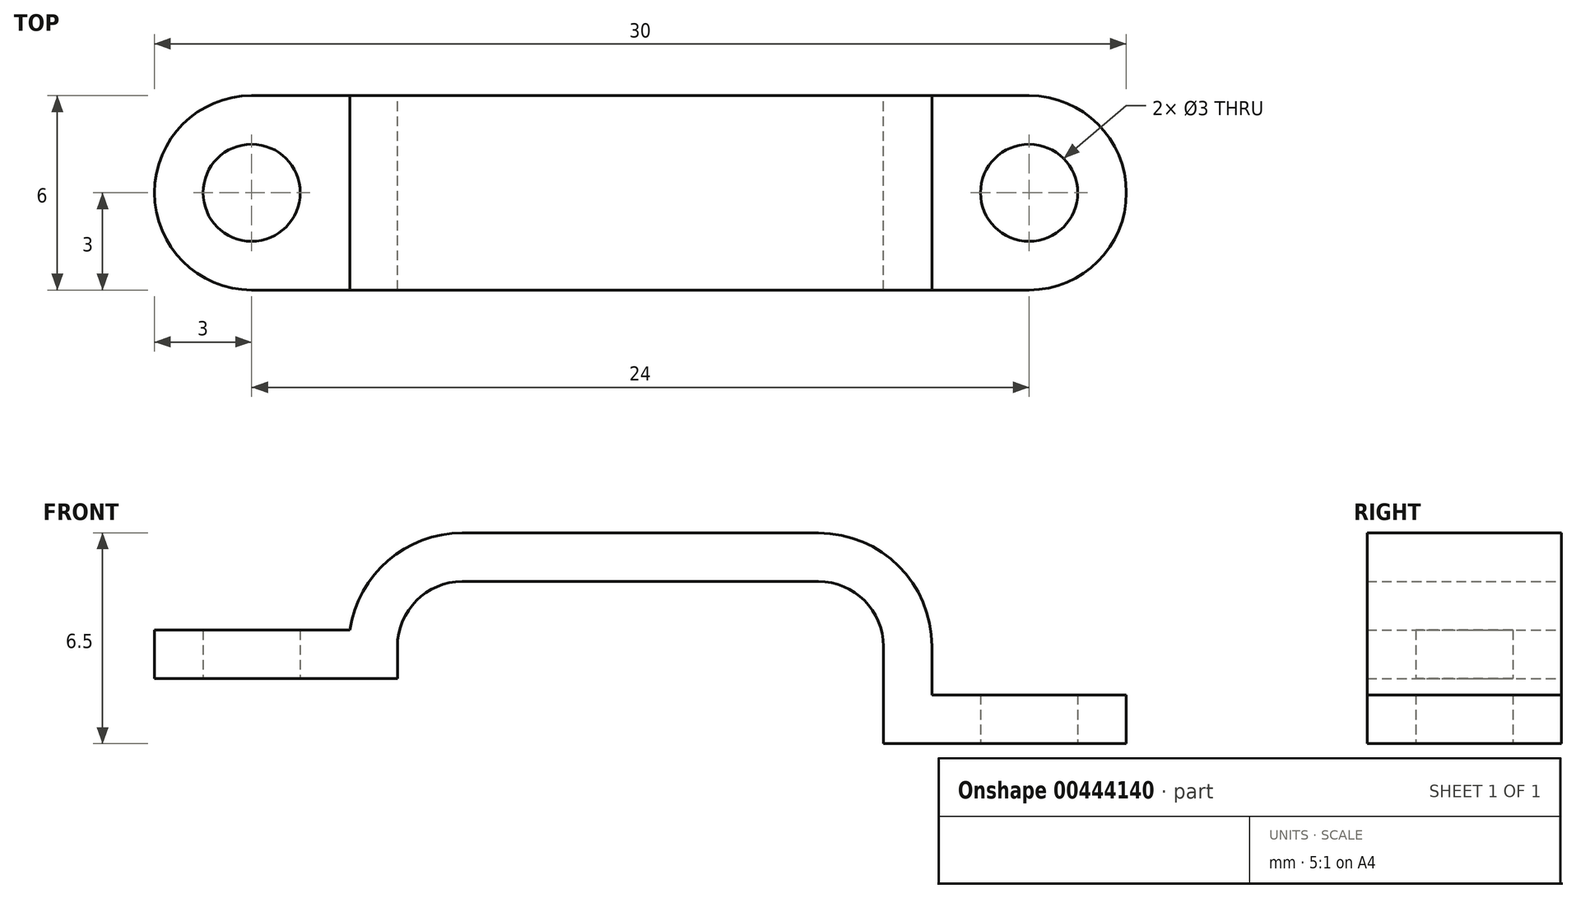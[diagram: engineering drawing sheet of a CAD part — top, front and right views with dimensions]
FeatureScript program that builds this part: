
annotation { "Feature Type Name" : "Feature", "Feature Type Description" : "" }
export const myFeature = defineFeature(function(context is Context, id is Id, definition is map)
    precondition{}
    {
        {
            var Q0;
            Q0=qCreatedBy(makeId("Front.planeOp"),FACE);
            var sketch = newSketch(context, id + "F0", { "sketchPlane" : qUnion([Q0])});
            skLineSegment(sketch, "E0.bottom", {"start": v(0, 0) * mm, "end": v(15, 0) * mm});
            skLineSegment(sketch, "E0.top", {"start": v(2, 5) * mm, "end": v(13, 5) * mm});
            skLineSegment(sketch, "E0.left", {"start": v(0, 0) * mm, "end": v(0, 3) * mm});
            skLineSegment(sketch, "E0.right", {"start": v(15, 0) * mm, "end": v(15, 3) * mm});
            skPoint(sketch, "E1.visualSharp", {"position": v(0, 5) * mm});
            skArc(sketch, "E1.filletArc", {"start": v(2, 5) * mm, "mid": v(0.59, 4.41) * mm, "end": v(0, 3) * mm});
            skPoint(sketch, "E2.visualSharp", {"position": v(15, 5) * mm});
            skArc(sketch, "E2.filletArc", {"start": v(15, 3) * mm, "mid": v(14.41, 4.41) * mm, "end": v(13, 5) * mm});
            skLineSegment(sketch, "E3.0", {"start": v(16.5, 0) * mm, "end": v(16.5, 3) * mm});
            skLineSegment(sketch, "E3.1", {"start": v(-1.5, 0) * mm, "end": v(-1.5, 3) * mm});
            skArc(sketch, "E3.2", {"start": v(2, 6.5) * mm, "mid": v(-0.47, 5.47) * mm, "end": v(-1.5, 3) * mm});
            skLineSegment(sketch, "E3.3", {"start": v(2, 6.5) * mm, "end": v(13, 6.5) * mm});
            skArc(sketch, "E3.4", {"start": v(16.5, 3) * mm, "mid": v(15.47, 5.47) * mm, "end": v(13, 6.5) * mm});
            skLineSegment(sketch, "E4", {"start": v(-1.5, 0) * mm, "end": v(0, 0) * mm});
            skLineSegment(sketch, "E5", {"start": v(15, 0) * mm, "end": v(16.5, 0) * mm});
            skLineSegment(sketch, "E6", {"start": v(-1.5, 2) * mm, "end": v(0, 2) * mm});
            skSolve(sketch);
        }
        {
            var Q0;
            Q0=makeQuery(id+"F0.imprint","IMPRINT",FACE,{"disambiguationData":[TD([[makeQuery(id+"F0.imprint","IMPRINT",EDGE,{"derivedFrom":sQuery(id+"F0.wireOp",EDGE,"E0.top")}),1.0]])]});
            extrude(context, id + "F1", {"entities" : qUnion([Q0]), "depth" : 6 * mm});
        }
        {
            var Q0;
            Q0=qCreatedBy(makeId("Top.planeOp"),FACE);
            var sketch = newSketch(context, id + "F2", { "sketchPlane" : qUnion([Q0])});
            skPoint(sketch, "E7.0", {"position": v(16.5, -6) * mm});
            skPoint(sketch, "E8.0", {"position": v(16.5, 0) * mm});
            skPoint(sketch, "E9.0", {"position": v(-1.5, -6) * mm});
            skPoint(sketch, "E10.0", {"position": v(-1.5, 0) * mm});
            skLineSegment(sketch, "E11.bottom", {"start": v(-1.5, 0) * mm, "end": v(-4.5, 0) * mm});
            skLineSegment(sketch, "E11.top", {"start": v(-1.5, -6) * mm, "end": v(-4.5, -6) * mm});
            skLineSegment(sketch, "E11.left", {"start": v(-1.5, 0) * mm, "end": v(-1.5, -6) * mm});
            skLineSegment(sketch, "E11.right", {"start": v(-7.5, -3) * mm, "end": v(-7.5, -3) * mm});
            skPoint(sketch, "E12.visualSharp", {"position": v(-7.5, 0) * mm});
            skArc(sketch, "E12.filletArc", {"start": v(-4.5, 0) * mm, "mid": v(-6.62, -0.88) * mm, "end": v(-7.5, -3) * mm});
            skPoint(sketch, "E13.visualSharp", {"position": v(-7.5, -6) * mm});
            skArc(sketch, "E13.filletArc", {"start": v(-7.5, -3) * mm, "mid": v(-6.62, -5.12) * mm, "end": v(-4.5, -6) * mm});
            skLineSegment(sketch, "E14.bottom", {"start": v(16.5, -6) * mm, "end": v(19.5, -6) * mm});
            skLineSegment(sketch, "E14.top", {"start": v(16.5, 0) * mm, "end": v(19.5, 0) * mm});
            skLineSegment(sketch, "E14.left", {"start": v(16.5, -6) * mm, "end": v(16.5, 0) * mm});
            skLineSegment(sketch, "E14.right", {"start": v(22.5, -3) * mm, "end": v(22.5, -3) * mm});
            skPoint(sketch, "E15.visualSharp", {"position": v(22.5, -6) * mm});
            skArc(sketch, "E15.filletArc", {"start": v(19.5, -6) * mm, "mid": v(21.62, -5.12) * mm, "end": v(22.5, -3) * mm});
            skPoint(sketch, "E16.visualSharp", {"position": v(22.5, 0) * mm});
            skArc(sketch, "E16.filletArc", {"start": v(22.5, -3) * mm, "mid": v(21.62, -0.88) * mm, "end": v(19.5, 0) * mm});
            skCircle(sketch, "E17", {"center": v(-4.5, -3) * mm, "radius": 1.5 * mm});
            skCircle(sketch, "E18", {"center": v(19.5, -3) * mm, "radius": 1.5 * mm});
            skSolve(sketch);
        }
        {
            var Q0;
            Q0=makeQuery(id+"F2.imprint","IMPRINT",FACE,{"disambiguationData":[TD([[makeQuery(id+"F2.imprint","IMPRINT",EDGE,{"derivedFrom":sQuery(id+"F2.wireOp",EDGE,"E14.bottom")}),1.0]])]});
            extrude(context, id + "F3", {"entities" : qUnion([Q0]), "operationType" : NewBodyOperationType.ADD, "depth" : 1.5 * mm});
        }
        {
            var Q0;
            Q0=makeQuery(id+"F1.opExtrude","SWEPT_FACE",FACE,{"disambiguationData":[OSD([sQuery(id+"F0.wireOp",EDGE,"E6")])]});
            var sketch = newSketch(context, id + "F4", { "sketchPlane" : qUnion([Q0])});
            skLineSegment(sketch, "E19.0.0", {"start": v(-4.5, 6) * mm, "end": v(-1.5, 6) * mm});
            skLineSegment(sketch, "E19.0.1", {"start": v(-1.5, 6) * mm, "end": v(-1.5, 0) * mm});
            skLineSegment(sketch, "E19.0.2", {"start": v(-1.5, 0) * mm, "end": v(-4.5, 0) * mm});
            skArc(sketch, "E19.0.3", {"start": v(-4.5, 0) * mm, "mid": v(-6.62, 0.88) * mm, "end": v(-7.5, 3) * mm});
            skArc(sketch, "E19.0.4", {"start": v(-7.5, 3) * mm, "mid": v(-6.62, 5.12) * mm, "end": v(-4.5, 6) * mm});
            skCircle(sketch, "E20.0", {"center": v(-4.5, 3) * mm, "radius": 1.5 * mm});
            skSolve(sketch);
        }
        {
            var Q0;
            Q0=makeQuery(id+"F4.imprint","IMPRINT",FACE,{"disambiguationData":[TD([[makeQuery(id+"F4.imprint","IMPRINT",EDGE,{"derivedFrom":sQuery(id+"F4.wireOp",EDGE,"E19.0.0")}),-1.0]])]});
            var Q1;
            Q1=makeQuery(id+"F4.imprint","IMPRINT",FACE,{"disambiguationData":[TD([[makeQuery(id+"F4.imprint","IMPRINT",EDGE,{"derivedFrom":sQuery(id+"F4.wireOp",EDGE,"E19.0.1")}),1.0]])]});
            extrude(context, id + "F5", {"entities" : qUnion([Q0, Q1]), "operationType" : NewBodyOperationType.ADD, "oppositeDirection" : true, "depth" : 1.5 * mm});
        }
    });
